# Revit family: hansgrohe_25032XXX-Rainfinity-Digital-Overhead-sho_NEW
name_source: partatom
category: Plumbing Fixtures
revit_build: Autodesk Revit 2015 (Build: 20140903_1530(x64)
units: mm (PartAtom-declared; Revit-internal decimal feet)

## types (2) — shared parameters
Always visible = Yes
Brand url = http://www.hansgrohe-int.com
Design country = Germany
Edition number = 1
GTIN code = https://4059625269060
IFC Classification = Sanitary Terminal
Installation instructions = https://www.hansgrohe.de
Manufacturer country = Germany
Manufacturer name = hansgrohe
Material 2 = Hansgrohe - Rainfinity Digital - Graphite
Product Guid = a6932486-14db-455e-bc49-d0880a0efd50
Product SKU = 25032XXX
Product data url = https://bimobject.com
Product name = 25032XXX Rainfinity Digital Overhead shower 360 3jet with wall connector
Product url = https://www.hansgrohe.de
QR code = http://bimobject.com
Technical description = https://www.hansgrohe.de

## per-type parameters (varying)
| type | Material 1 |
| 700 Matt White | Hansgrohe - Rainfinity Digital - 700 Matt White |
| 000 Chrome | Hansgrohe - Rainfinity Digital - 000 Chrome |

## geometry (parser evidence)
native form markers: Sweep x3
no freeform markers — native parametric forms only
